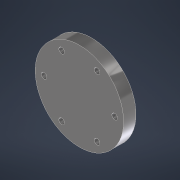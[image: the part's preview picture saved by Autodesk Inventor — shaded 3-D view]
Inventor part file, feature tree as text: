
AUTODESK INVENTOR PART (.ipt)
format: ipt  version: 2022 (Build 260153000, 153)  size: 153,600 bytes
history: native  units: mm
features: sketch x4, projected_geometry x3, extrude x2, hole x2, reference x2, other x2, chamfer x1, plane x1
ambient origin geometry x8: Origin, YZ Plane, XZ Plane, XY Plane, X Axis, Y Axis, Z Axis, Center Point
bodies: Solid1 (feature_tree)
feature tree (17):
  extrude  "Extrusion1"  Depth=10.0mm
  extrude  "Extrusion2"  Depth=2.0mm TaperAngle=0.0deg
  chamfer  "Chamfer1"  Distance=3.0mm Angle=30.0deg
  plane  "Work Plane1"
  hole  "Hole2"  [1 undecoded]
  hole  "Hole3"  [1 undecoded]
  sketch  "Sketch1"  dims[d0=10.0mm d1=0.0mm d2=4.0mm]
  reference  "Reference1"
  sketch  "Sketch2"  dims[d3=50.0mm d4=2.0mm d5=0.0mm d6=3.0mm d7=2.0mm d8=30.0deg]
  projected_geometry  "Projected Loop1"
  sketch  "Sketch4"  dims[d20=2.459mm d21=6.0mm d22=13.0mm d23=3.4mm d24=90.0deg d25=8.8mm d26=20.594885mm d27=5.0mm d28=0.0mm]
  reference  "Reference2"
  projected_geometry  "Projected Loop2"
  sketch  "Sketch5"  dims[d29=4.0mm d30=40.0mm d31=60.0mm d33=360.0deg d35=3.242mm d36=5.0mm d37=4.0mm d38=2.0mm d39=90.0deg d40=6.0mm d41=20.594885mm d32=0.872665mm]
  projected_geometry  "Projected Loop3"
  other  "SistemaDeElevación.iam"
  other  "Tornillo de elevación:1"
note: 2 required parameter values undecoded (feature->parameter linkage not recoverable at this tier; creation-order binding heuristic only, values carry confidence <= 0.55)
